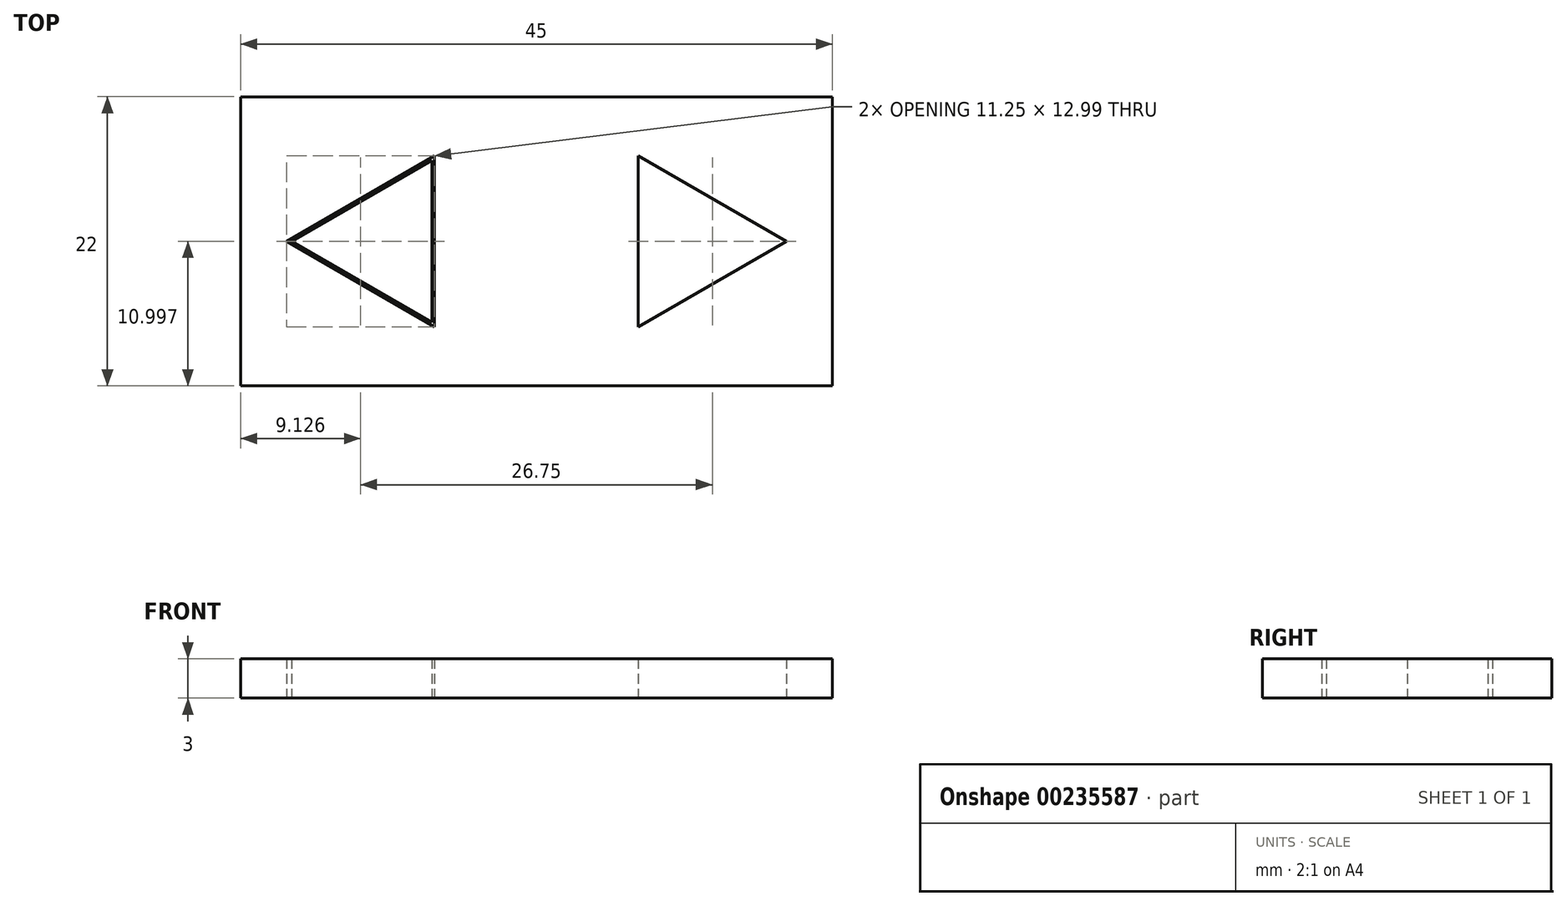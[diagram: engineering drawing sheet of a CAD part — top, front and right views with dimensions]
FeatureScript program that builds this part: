
annotation { "Feature Type Name" : "Feature", "Feature Type Description" : "" }
export const myFeature = defineFeature(function(context is Context, id is Id, definition is map)
    precondition{}
    {
        {
            var Q0;
            Q0=qCreatedBy(makeId("Top.planeOp"),FACE);
            var sketch = newSketch(context, id + "F0", { "sketchPlane" : qUnion([Q0])});
            skLineSegment(sketch, "E0.bottom", {"start": v(-22.33, 11.05) * mm, "end": v(22.67, 11.05) * mm});
            skLineSegment(sketch, "E0.top", {"start": v(-22.33, -10.95) * mm, "end": v(22.67, -10.95) * mm});
            skLineSegment(sketch, "E0.left", {"start": v(-22.33, 11.05) * mm, "end": v(-22.33, -10.95) * mm});
            skLineSegment(sketch, "E0.right", {"start": v(22.67, 11.05) * mm, "end": v(22.67, -10.95) * mm});
            skCircle(sketch, "E1.cCircle", {"center": v(-11.33, 0.05) * mm, "radius": 7.5 * mm, "construction": true});
            skLineSegment(sketch, "E1.0", {"start": v(-7.58, -6.45) * mm, "end": v(-18.83, 0.05) * mm});
            skLineSegment(sketch, "E1.1", {"start": v(-18.83, 0.05) * mm, "end": v(-7.58, 6.54) * mm});
            skLineSegment(sketch, "E1.2", {"start": v(-7.58, 6.54) * mm, "end": v(-7.58, -6.45) * mm});
            skLineSegment(sketch, "E2", {"start": v(0.17, 11.05) * mm, "end": v(0.17, -10.95) * mm, "construction": true});
            skLineSegment(sketch, "E3.MirrorCS", {"start": v(7.92, 6.54) * mm, "end": v(7.92, -6.45) * mm});
            skLineSegment(sketch, "E4.MirrorCS", {"start": v(19.17, 0.05) * mm, "end": v(7.92, 6.54) * mm});
            skLineSegment(sketch, "E5.MirrorCS", {"start": v(7.92, -6.45) * mm, "end": v(19.17, 0.05) * mm});
            skSolve(sketch);
        }
        {
            var Q0;
            Q0=makeQuery(id+"F0.imprint","IMPRINT",FACE,{"disambiguationData":[TD([[makeQuery(id+"F0.imprint","IMPRINT",EDGE,{"derivedFrom":sQuery(id+"F0.wireOp",EDGE,"E0.bottom")}),-1.0]])]});
            extrude(context, id + "F1", {"entities" : qUnion([Q0]), "depth" : 3 * mm});
        }
        {
            var Q0;
            Q0=makeQuery(id+"F0.imprint","IMPRINT",FACE,{"disambiguationData":[TD([[makeQuery(id+"F0.imprint","IMPRINT",EDGE,{"derivedFrom":sQuery(id+"F0.wireOp",EDGE,"E0.bottom")}),-1.0]])]});
            var sketch = newSketch(context, id + "F2", { "sketchPlane" : qUnion([Q0])});
            skLineSegment(sketch, "E6.0", {"start": v(-7.78, -6.1) * mm, "end": v(-18.43, 0.05) * mm});
            skLineSegment(sketch, "E6.1", {"start": v(-7.78, 6.2) * mm, "end": v(-7.78, -6.1) * mm});
            skLineSegment(sketch, "E6.2", {"start": v(-18.43, 0.05) * mm, "end": v(-7.78, 6.2) * mm});
            skSolve(sketch);
        }
        {
            var Q0;
            Q0 = qSketchRegion(id + "F2", true);
            extrude(context, id + "F3", {"entities" : qUnion([Q0]), "depth" : 3 * mm});
        }
    });
